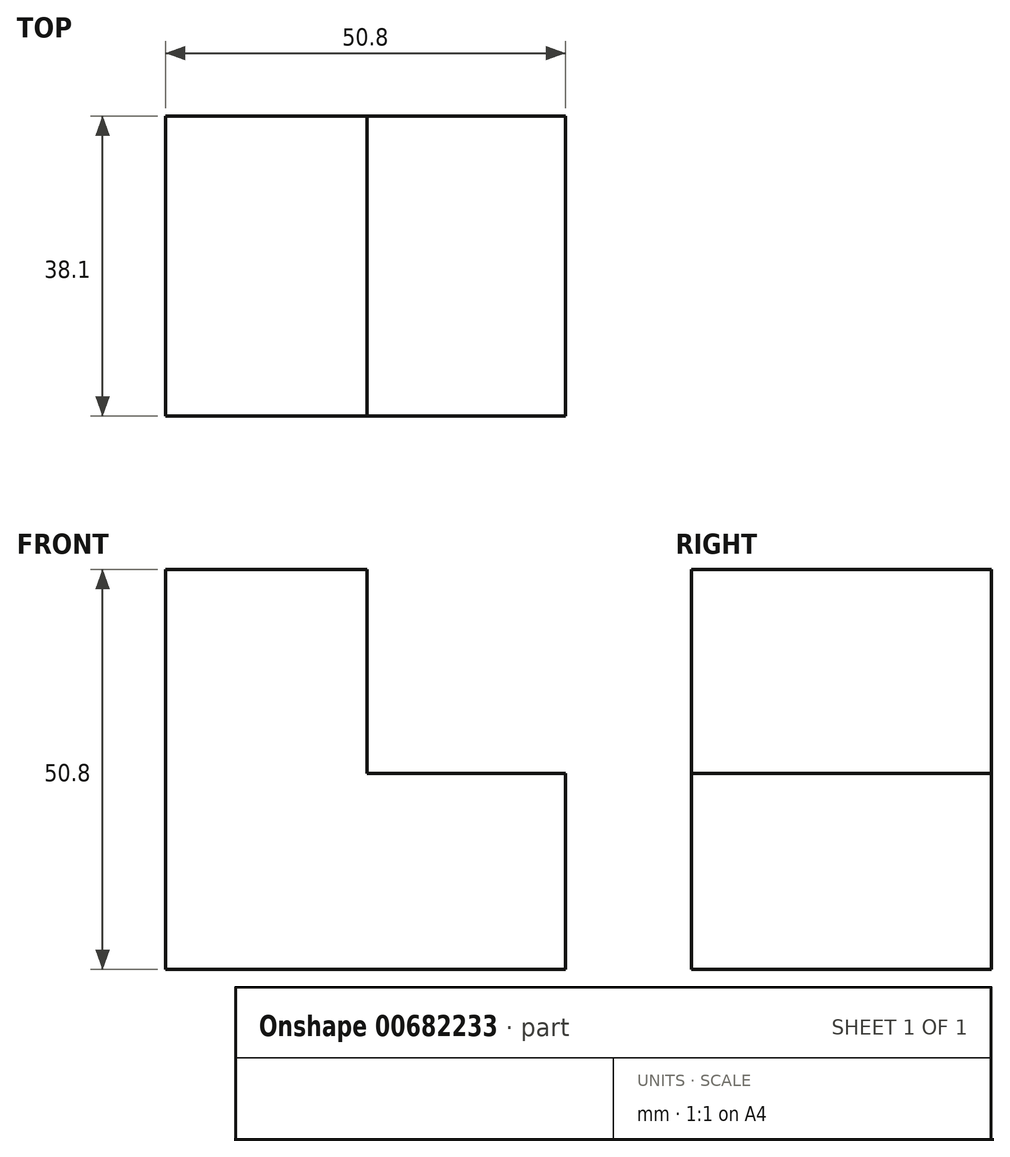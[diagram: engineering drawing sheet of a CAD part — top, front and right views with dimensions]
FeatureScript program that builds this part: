
annotation { "Feature Type Name" : "Feature", "Feature Type Description" : "" }
export const myFeature = defineFeature(function(context is Context, id is Id, definition is map)
    precondition{}
    {
        {
            var Q0;
            Q0=qCreatedBy(makeId("Front.planeOp"),FACE);
            var sketch = newSketch(context, id + "F0", { "sketchPlane" : qUnion([Q0])});
            skLineSegment(sketch, "E0", {"start": v(0, 0) * mm, "end": v(-50.8, 0) * mm});
            skLineSegment(sketch, "E1", {"start": v(-50.8, 0) * mm, "end": v(-50.8, 50.8) * mm});
            skLineSegment(sketch, "E2", {"start": v(-50.8, 50.8) * mm, "end": v(-25.18, 50.8) * mm});
            skLineSegment(sketch, "E3", {"start": v(-25.18, 50.8) * mm, "end": v(-25.18, 24.9) * mm});
            skLineSegment(sketch, "E4", {"start": v(-25.18, 24.9) * mm, "end": v(0, 24.9) * mm});
            skLineSegment(sketch, "E5", {"start": v(0, 24.9) * mm, "end": v(0, 0) * mm});
            skSolve(sketch);
        }
        {
            var Q0;
            Q0=makeQuery(id+"F0.imprint","IMPRINT",FACE,{"disambiguationData":[TD([[makeQuery(id+"F0.imprint","IMPRINT",EDGE,{"derivedFrom":sQuery(id+"F0.wireOp",EDGE,"E0")}),-1.0]])]});
            extrude(context, id + "F1", {"entities" : qUnion([Q0]), "depth" : 38.1 * mm, "offsetDistance" : 25.4 * mm});
        }
    });
